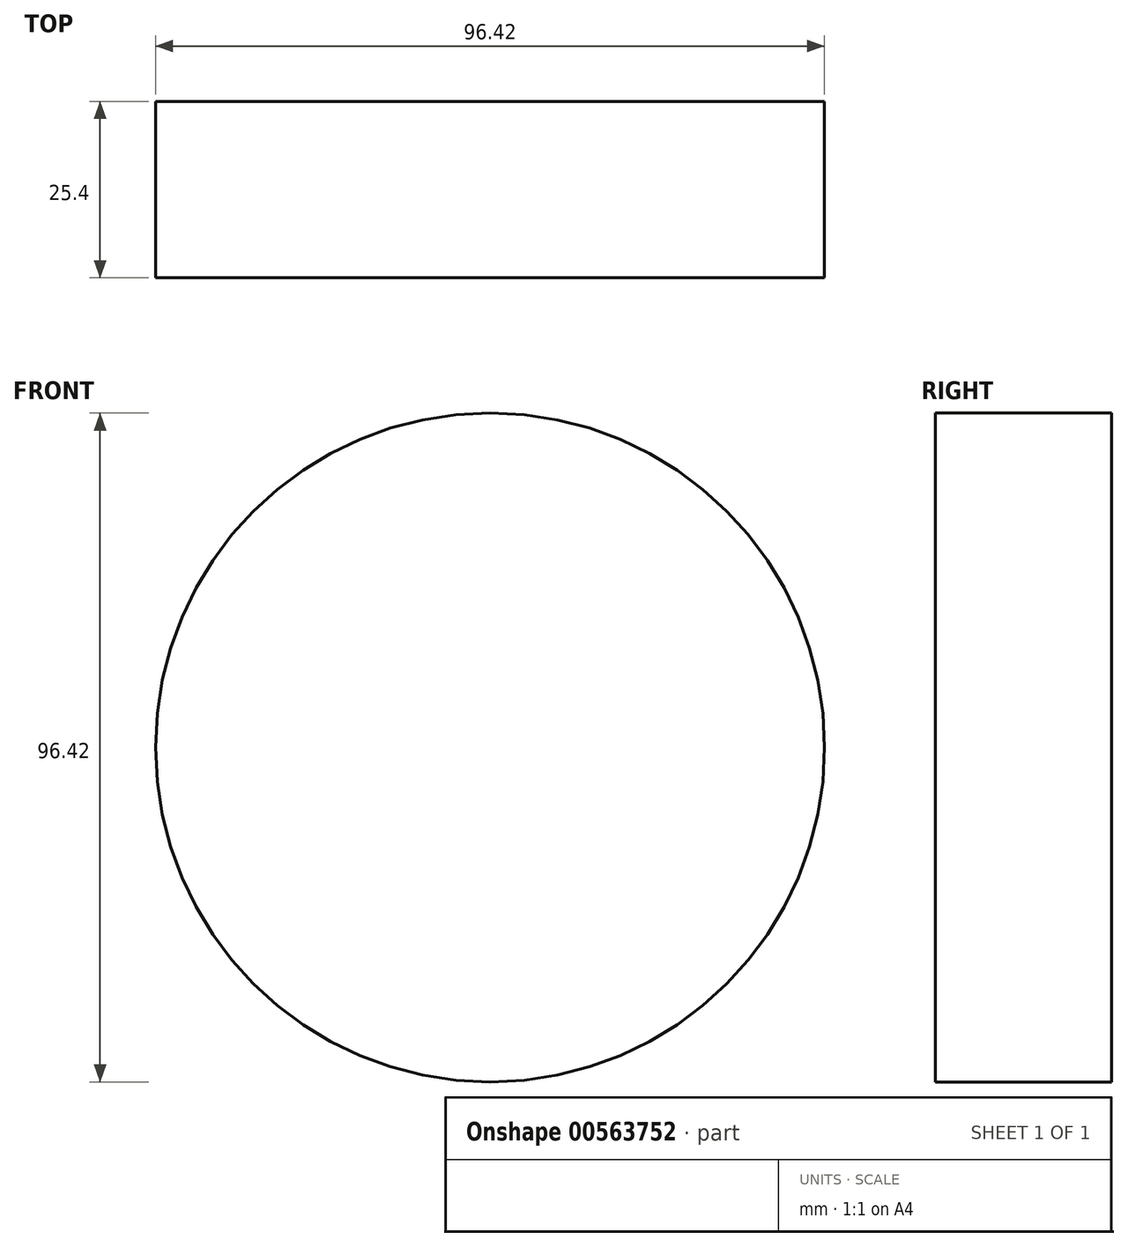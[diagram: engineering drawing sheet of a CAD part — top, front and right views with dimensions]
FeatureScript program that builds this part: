
annotation { "Feature Type Name" : "Feature", "Feature Type Description" : "" }
export const myFeature = defineFeature(function(context is Context, id is Id, definition is map)
    precondition{}
    {
        {
            var Q0;
            Q0=qCreatedBy(makeId("Front.planeOp"),FACE);
            var sketch = newSketch(context, id + "F0", { "sketchPlane" : qUnion([Q0])});
            skCircle(sketch, "E0", {"center": v(0, 0) * mm, "radius": 48.21 * mm});
            skSolve(sketch);
        }
        {
            var Q0;
            Q0=makeQuery(id+"F0.imprint","IMPRINT",FACE,{"disambiguationData":[TD([[makeQuery(id+"F0.imprint","IMPRINT",EDGE,{"derivedFrom":sQuery(id+"F0.wireOp",EDGE,"E0")}),1.0]])]});
            extrude(context, id + "F1", {"entities" : qUnion([Q0]), "oppositeDirection" : true, "depth" : 25.4 * mm, "offsetDistance" : 25.4 * mm});
        }
    });
